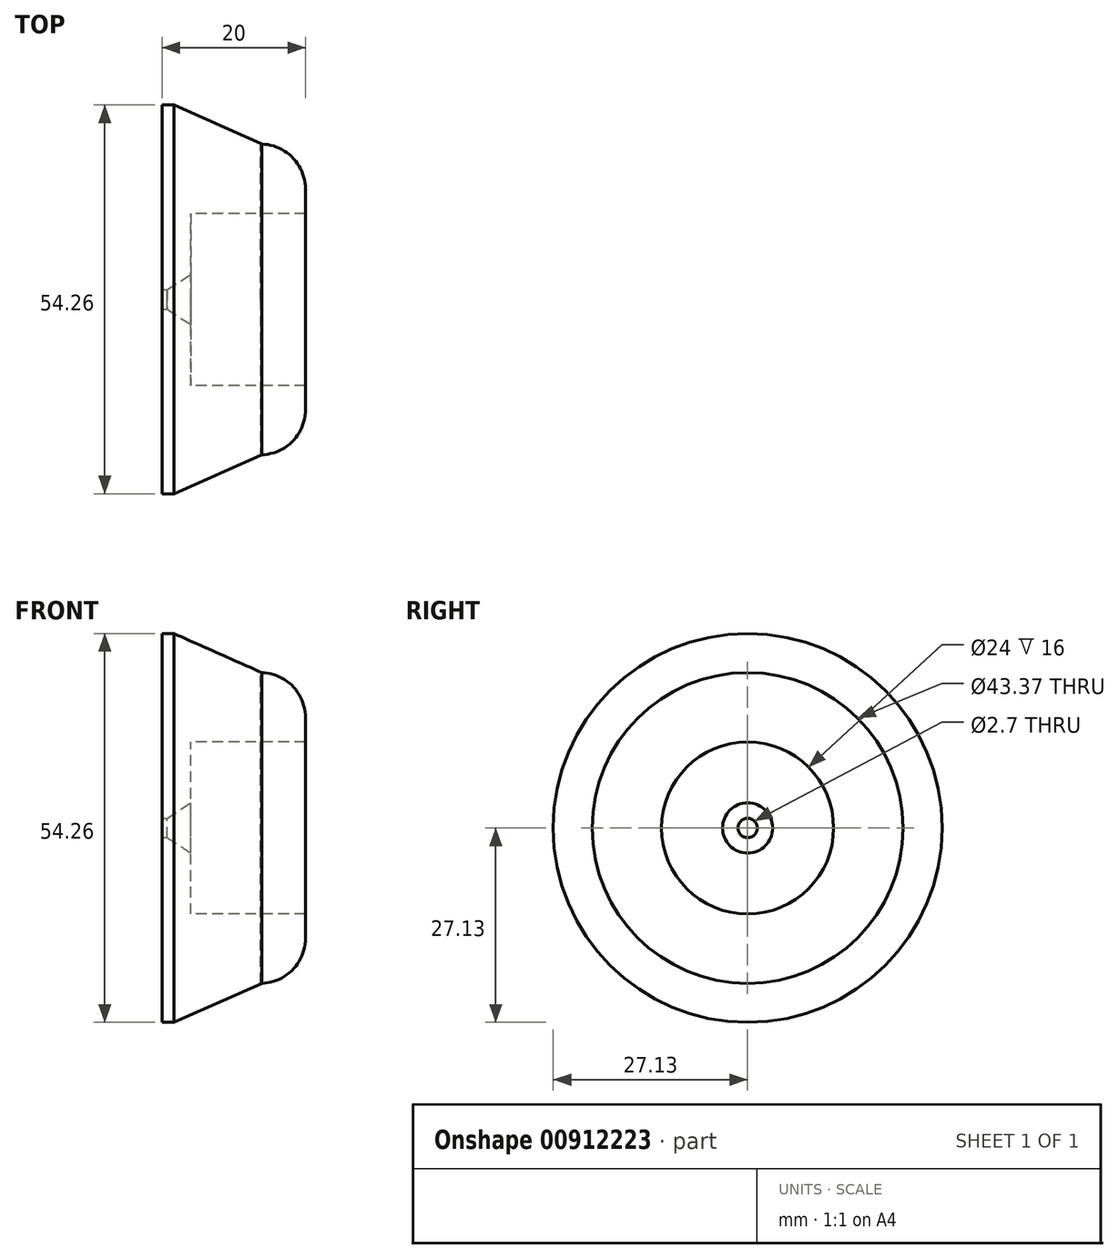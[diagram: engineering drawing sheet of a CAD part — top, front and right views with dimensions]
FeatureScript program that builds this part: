
annotation { "Feature Type Name" : "Feature", "Feature Type Description" : "" }
export const myFeature = defineFeature(function(context is Context, id is Id, definition is map)
    precondition{}
    {
        {
            var Q0;
            Q0=qCreatedBy(makeId("Right.planeOp"),FACE);
            var sketch = newSketch(context, id + "F0", { "sketchPlane" : qUnion([Q0])});
            skCircle(sketch, "E0", {"center": v(0, 0) * mm, "radius": 12 * mm});
            skCircle(sketch, "E1", {"center": v(0, 0) * mm, "radius": 30 * mm});
            skCircle(sketch, "E2", {"center": v(0, 0) * mm, "radius": 15.18 * mm});
            skCircle(sketch, "E3", {"center": v(0, 0) * mm, "radius": 27.13 * mm});
            skCircle(sketch, "E4", {"center": v(0, 0) * mm, "radius": 21.68 * mm});
            skCircle(sketch, "E5", {"center": v(0, 0) * mm, "radius": 1.77 * mm});
            skSolve(sketch);
        }
        {
            var Q0;
            Q0=makeQuery(id+"F0.imprint","IMPRINT",FACE,{"disambiguationData":[TD([[makeQuery(id+"F0.imprint","IMPRINT",EDGE,{"derivedFrom":sQuery(id+"F0.wireOp",EDGE,"E0")}),-1.0]])]});
            extrude(context, id + "F1", {"entities" : qUnion([Q0]), "depth" : 20 * mm, "offsetDistance" : 25 * mm});
        }
        {
            var Q0;
            Q0=makeQuery(id+"F0.imprint","IMPRINT",FACE,{"disambiguationData":[TD([[makeQuery(id+"F0.imprint","IMPRINT",EDGE,{"derivedFrom":sQuery(id+"F0.wireOp",EDGE,"E2")}),-1.0]])]});
            extrude(context, id + "F2", {"entities" : qUnion([Q0]), "operationType" : NewBodyOperationType.ADD, "depth" : 20 * mm, "offsetDistance" : 25 * mm});
        }
        {
            var Q0;
            Q0=makeQuery(id+"F2.opExtrude","CAP_EDGE",EDGE,{"disambiguationData":[OSD([sQuery(id+"F0.wireOp",EDGE,"E4")])],"isStart":false});
            fillet(context, id + "F3", {"entities" : qUnion([Q0]), "radius" : 6.3 * mm, "tangentPropagation" : true, "allowEdgeOverflow" : false});
        }
        {
            var Q0;
            Q0=makeQuery(id+"F0.imprint","IMPRINT",FACE,{"disambiguationData":[TD([[makeQuery(id+"F0.imprint","IMPRINT",EDGE,{"derivedFrom":sQuery(id+"F0.wireOp",EDGE,"E3")}),1.0]])]});
            extrude(context, id + "F4", {"entities" : qUnion([Q0]), "operationType" : NewBodyOperationType.ADD, "depth" : 14 * mm, "offsetDistance" : 25 * mm});
        }
        {
            var Q0;
            Q0=makeQuery(id+"F4.opExtrude","CAP_EDGE",EDGE,{"disambiguationData":[OSD([sQuery(id+"F0.wireOp",EDGE,"E3")])],"isStart":false});
            chamfer(context, id + "F5", {"entities" : qUnion([Q0]), "chamferType" : ChamferType.OFFSET_ANGLE, "width" : 5.5 * mm, "oppositeDirection" : false, "angle" : 66 * degree, "tangentPropagation" : true});
        }
        {
            var Q0;
            Q0=makeQuery(id+"F0.imprint","IMPRINT",FACE,{"disambiguationData":[TD([[makeQuery(id+"F0.imprint","IMPRINT",EDGE,{"derivedFrom":sQuery(id+"F0.wireOp",EDGE,"E0")}),1.0]])]});
            var Q1;
            Q1=makeQuery(id+"F0.imprint","IMPRINT",FACE,{"disambiguationData":[TD([[makeQuery(id+"F0.imprint","IMPRINT",EDGE,{"derivedFrom":sQuery(id+"F0.wireOp",EDGE,"E5")}),1.0]])]});
            extrude(context, id + "F6", {"entities" : qUnion([Q0, Q1]), "operationType" : NewBodyOperationType.ADD, "depth" : 4 * mm, "offsetDistance" : 25 * mm});
        }
        {
            var Q0;
            Q0=makeQuery(id+"F6.opExtrude","CAP_FACE",FACE,{"disambiguationData":[OSD([sQuery(id+"F0.wireOp",EDGE,"E0")])],"isStart":false});
            var sketch = newSketch(context, id + "F7", { "sketchPlane" : qUnion([Q0])});
            skPoint(sketch, "E6", {"position": v(0, 0) * mm});
            skSolve(sketch);
        }
        {
            var Q0;
            Q0=sQuery(id+"F7.wireOp",VERTEX,"E6");
            var Q1;
            Q1=makeQuery(id+"F1.opExtrude","SWEPT_BODY",BODY,{"disambiguationData":[OSD([sQuery(id+"F0.wireOp",EDGE,"E0"),sQuery(id+"F0.wireOp",EDGE,"E2")])]});
            hole(context, id + "F8", {"style" : HoleStyle.C_SINK, "endStyle" : HoleEndStyle.BLIND, "holeDiameter" : 2.7 * mm, "cSinkDiameter" : 7 * mm, "cSinkAngle" : 66 * degree, "majorDiameter" : 5 * mm, "holeDepth" : 12 * mm, "isTappedThrough" : true, "tappedDepth" : 12 * mm, "tapClearance" : 3, "locations" : qUnion([Q0]), "scope" : qUnion([Q1])});
        }
    });
